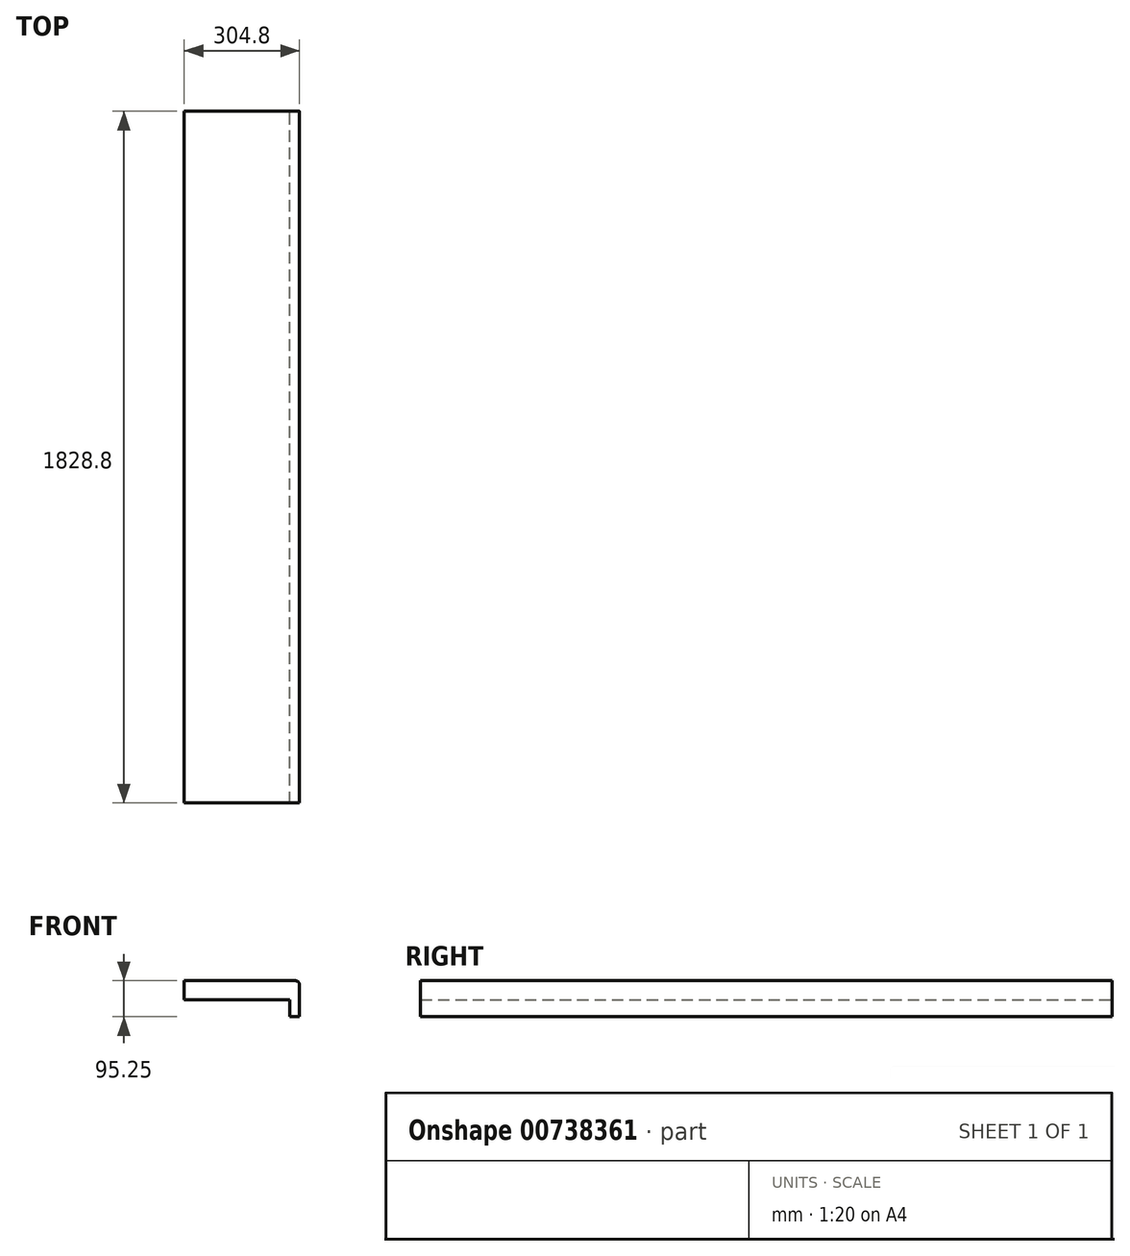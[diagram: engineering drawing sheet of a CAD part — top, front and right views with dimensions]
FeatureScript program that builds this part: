
annotation { "Feature Type Name" : "Feature", "Feature Type Description" : "" }
export const myFeature = defineFeature(function(context is Context, id is Id, definition is map)
    precondition{}
    {
        {
            var Q0;
            Q0=qCreatedBy(makeId("Front.planeOp"),FACE);
            var sketch = newSketch(context, id + "F0", { "sketchPlane" : qUnion([Q0])});
            skLineSegment(sketch, "E0", {"start": v(-96.7, 95.25) * mm, "end": v(-96.7, 44.45) * mm});
            skLineSegment(sketch, "E1", {"start": v(-96.7, 44.45) * mm, "end": v(182.7, 44.45) * mm});
            skLineSegment(sketch, "E2", {"start": v(182.7, 44.45) * mm, "end": v(182.7, 0) * mm});
            skLineSegment(sketch, "E3", {"start": v(208.1, 0) * mm, "end": v(182.7, 0) * mm});
            skLineSegment(sketch, "E4", {"start": v(-96.7, 95.25) * mm, "end": v(197, 95.25) * mm});
            skLineSegment(sketch, "E5", {"start": v(208.1, 84.14) * mm, "end": v(208.1, 0) * mm});
            skPoint(sketch, "E6.visualSharp", {"position": v(208.1, 95.25) * mm});
            skArc(sketch, "E6.filletArc", {"start": v(208.1, 84.14) * mm, "mid": v(204.85, 92) * mm, "end": v(197, 95.25) * mm});
            skSolve(sketch);
        }
        {
            var Q0;
            Q0=makeQuery(id+"F0.imprint","IMPRINT",FACE,{"disambiguationData":[TD([[makeQuery(id+"F0.imprint","IMPRINT",EDGE,{"derivedFrom":sQuery(id+"F0.wireOp",EDGE,"E0")}),1.0]])]});
            extrude(context, id + "F1", {"entities" : qUnion([Q0]), "depth" : 1828.8 * mm, "offsetDistance" : 25.4 * mm});
        }
    });
